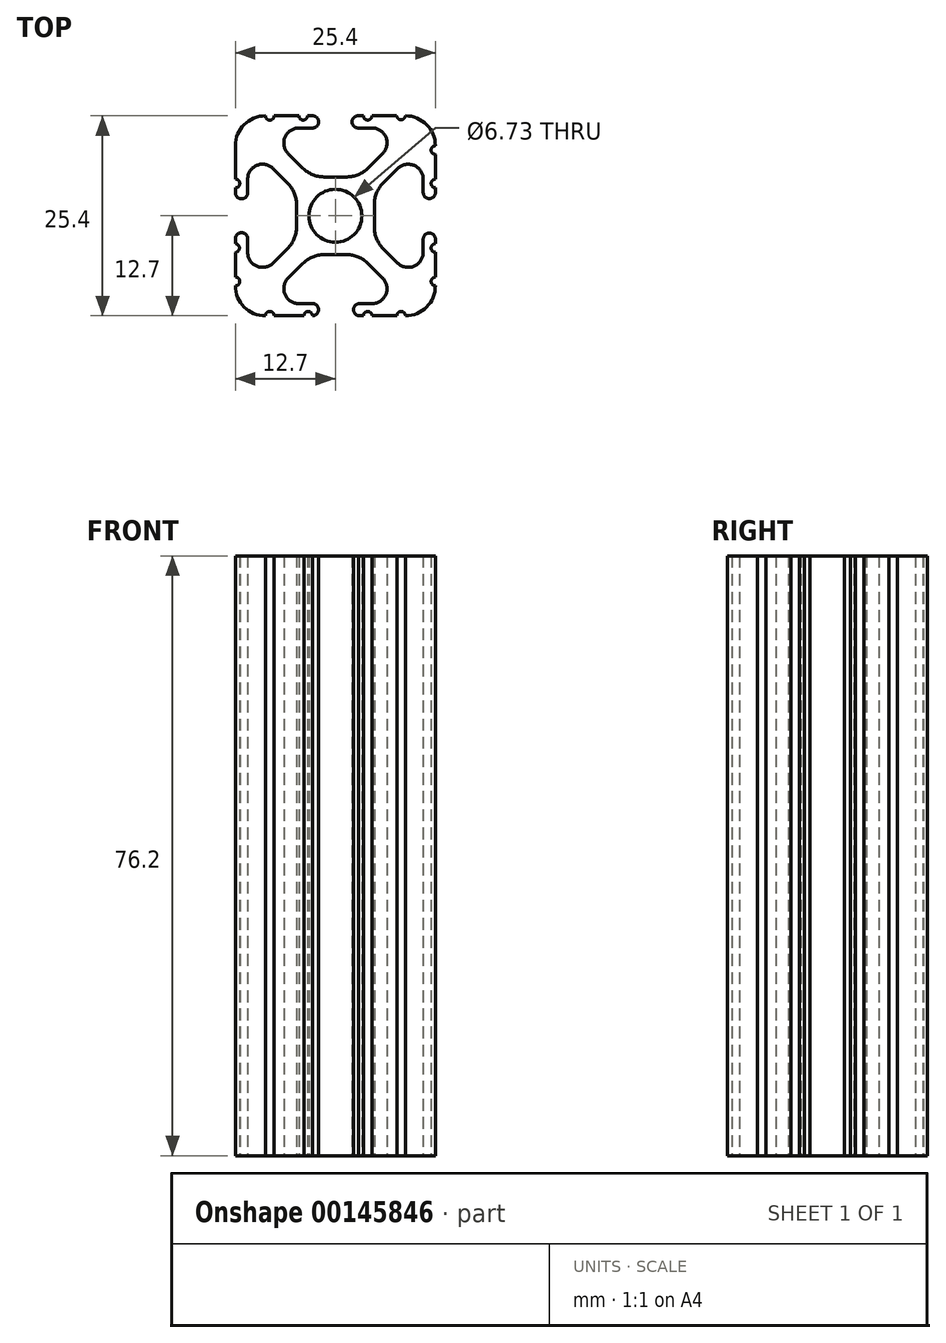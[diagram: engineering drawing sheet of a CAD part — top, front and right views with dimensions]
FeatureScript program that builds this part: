
annotation { "Feature Type Name" : "Feature", "Feature Type Description" : "" }
export const myFeature = defineFeature(function(context is Context, id is Id, definition is map)
    precondition{}
    {
        {
            var Q0;
            Q0=qCreatedBy(makeId("Top.planeOp"),FACE);
            var sketch = newSketch(context, id + "F0", { "sketchPlane" : qUnion([Q0])});
            skCircle(sketch, "E0", {"center": v(-12.7, 12.7) * mm, "radius": 3.36 * mm});
            skLineSegment(sketch, "E1.bottom", {"start": v(-11.24, 17.64) * mm, "end": v(-14.16, 17.64) * mm});
            skLineSegment(sketch, "E1.top", {"start": v(-11.24, 7.76) * mm, "end": v(-14.16, 7.76) * mm});
            skLineSegment(sketch, "E1.left", {"start": v(-7.76, 14.16) * mm, "end": v(-7.76, 11.24) * mm});
            skLineSegment(sketch, "E1.right", {"start": v(-17.64, 14.16) * mm, "end": v(-17.64, 11.24) * mm});
            skPoint(sketch, "E2.visualSharp", {"position": v(-25.4, 25.4) * mm});
            skPoint(sketch, "E3.visualSharp", {"position": v(0, 25.4) * mm});
            skPoint(sketch, "E4.visualSharp", {"position": v(0, 0) * mm});
            skPoint(sketch, "E5.visualSharp", {"position": v(-25.4, 0) * mm});
            skLineSegment(sketch, "E6.0", {"start": v(-18.7, 20.6) * mm, "end": v(-16.85, 18.76) * mm});
            skLineSegment(sketch, "E7.0", {"start": v(-20.6, 18.7) * mm, "end": v(-18.76, 16.85) * mm});
            skPoint(sketch, "E8.orphan", {"position": v(-23.85, 1.55) * mm});
            skPoint(sketch, "E9.orphan", {"position": v(-23.85, 23.85) * mm});
            skPoint(sketch, "E10.orphan", {"position": v(-1.55, 23.85) * mm});
            skPoint(sketch, "E11.orphan", {"position": v(-1.55, 1.55) * mm});
            skLineSegment(sketch, "E12", {"start": v(-8.55, 6.64) * mm, "end": v(-6.7, 4.8) * mm});
            skLineSegment(sketch, "E13.0", {"start": v(-18.7, 4.8) * mm, "end": v(-16.85, 6.64) * mm});
            skLineSegment(sketch, "E14.0", {"start": v(-20.6, 6.7) * mm, "end": v(-18.76, 8.55) * mm});
            skLineSegment(sketch, "E15.0", {"start": v(-8.55, 18.76) * mm, "end": v(-6.7, 20.6) * mm});
            skPoint(sketch, "E16.visualSharp", {"position": v(-23.85, 21.95) * mm});
            skArc(sketch, "E16.filletArc", {"start": v(-20.6, 18.7) * mm, "mid": v(-22.68, 19.1) * mm, "end": v(-23.85, 17.35) * mm});
            skPoint(sketch, "E17.visualSharp", {"position": v(-21.95, 23.85) * mm});
            skArc(sketch, "E17.filletArc", {"start": v(-17.35, 23.85) * mm, "mid": v(-19.1, 22.68) * mm, "end": v(-18.7, 20.6) * mm});
            skPoint(sketch, "E18.visualSharp", {"position": v(-5.34, 23.85) * mm});
            skLineSegment(sketch, "E19", {"start": v(-17.35, 23.85) * mm, "end": v(-15.58, 23.85) * mm});
            skLineSegment(sketch, "E20", {"start": v(-23.85, 17.35) * mm, "end": v(-23.85, 15.62) * mm});
            skLineSegment(sketch, "E21", {"start": v(-8.05, 1.55) * mm, "end": v(-9.78, 1.55) * mm});
            skArc(sketch, "E22.filletArc", {"start": v(-6.7, 20.6) * mm, "mid": v(-6.3, 22.68) * mm, "end": v(-8.05, 23.85) * mm});
            skPoint(sketch, "E23.visualSharp", {"position": v(-1.55, 3.45) * mm});
            skPoint(sketch, "E24.visualSharp", {"position": v(-3.45, 1.55) * mm});
            skArc(sketch, "E24.filletArc", {"start": v(-8.05, 1.55) * mm, "mid": v(-6.3, 2.73) * mm, "end": v(-6.7, 4.8) * mm});
            skArc(sketch, "E25.filletArc", {"start": v(-18.7, 4.8) * mm, "mid": v(-19.1, 2.73) * mm, "end": v(-17.35, 1.55) * mm});
            skArc(sketch, "E26.filletArc", {"start": v(-23.85, 8.05) * mm, "mid": v(-22.68, 6.3) * mm, "end": v(-20.6, 6.7) * mm});
            skLineSegment(sketch, "E27.bottom", {"start": v(-4.9, 0) * mm, "end": v(-8.05, 0) * mm});
            skLineSegment(sketch, "E27.top", {"start": v(-4.92, 25.4) * mm, "end": v(-8.05, 25.4) * mm});
            skLineSegment(sketch, "E27.left", {"start": v(0, 4.9) * mm, "end": v(0, 8.05) * mm});
            skLineSegment(sketch, "E27.right", {"start": v(-25.4, 4.9) * mm, "end": v(-25.4, 8.05) * mm});
            skArc(sketch, "E28.filletArc", {"start": v(-25.4, 3.81) * mm, "mid": v(-24.28, 1.12) * mm, "end": v(-21.59, 0) * mm});
            skArc(sketch, "E29.filletArc", {"start": v(-3.81, 0) * mm, "mid": v(-1.12, 1.12) * mm, "end": v(0, 3.8) * mm});
            skArc(sketch, "E30.filletArc", {"start": v(0, 21.59) * mm, "mid": v(-1.12, 24.28) * mm, "end": v(-3.8, 25.4) * mm});
            skArc(sketch, "E31.filletArc", {"start": v(-21.59, 25.4) * mm, "mid": v(-24.28, 24.28) * mm, "end": v(-25.4, 21.59) * mm});
            skPoint(sketch, "E32.newPointA", {"position": v(-17.64, 7.76) * mm});
            skArc(sketch, "E32.filletArc", {"start": v(-14.16, 7.76) * mm, "mid": v(-15.62, 7.47) * mm, "end": v(-16.85, 6.64) * mm});
            skPoint(sketch, "E33.newPointA", {"position": v(-7.76, 7.76) * mm});
            skArc(sketch, "E33.filletArc", {"start": v(-8.55, 6.64) * mm, "mid": v(-9.78, 7.47) * mm, "end": v(-11.24, 7.76) * mm});
            skArc(sketch, "E34.filletArc", {"start": v(-7.76, 11.24) * mm, "mid": v(-7.47, 9.78) * mm, "end": v(-6.64, 8.55) * mm});
            skArc(sketch, "E35.filletArc", {"start": v(-6.64, 16.85) * mm, "mid": v(-7.47, 15.62) * mm, "end": v(-7.76, 14.16) * mm});
            skPoint(sketch, "E36.newPointB", {"position": v(-7.76, 17.64) * mm});
            skArc(sketch, "E36.filletArc", {"start": v(-11.24, 17.64) * mm, "mid": v(-9.78, 17.93) * mm, "end": v(-8.55, 18.76) * mm});
            skPoint(sketch, "E37.newPointB", {"position": v(-17.64, 17.64) * mm});
            skArc(sketch, "E37.filletArc", {"start": v(-16.85, 18.76) * mm, "mid": v(-15.62, 17.93) * mm, "end": v(-14.16, 17.64) * mm});
            skArc(sketch, "E38.filletArc", {"start": v(-17.64, 14.16) * mm, "mid": v(-17.93, 15.62) * mm, "end": v(-18.76, 16.85) * mm});
            skArc(sketch, "E39.filletArc", {"start": v(-18.76, 8.55) * mm, "mid": v(-17.93, 9.78) * mm, "end": v(-17.64, 11.24) * mm});
            skLineSegment(sketch, "E40", {"start": v(-6.64, 8.55) * mm, "end": v(-4.8, 6.7) * mm});
            skPoint(sketch, "E41.visualSharp", {"position": v(-1.55, 21.95) * mm});
            skArc(sketch, "E42.filletArc", {"start": v(-4.8, 6.7) * mm, "mid": v(-2.73, 6.3) * mm, "end": v(-1.55, 8.05) * mm});
            skLineSegment(sketch, "E43", {"start": v(-1.55, 8.05) * mm, "end": v(-1.55, 9.78) * mm});
            skLineSegment(sketch, "E44", {"start": v(-6.64, 16.85) * mm, "end": v(-4.8, 18.7) * mm});
            skArc(sketch, "E45.filletArc", {"start": v(-1.55, 17.35) * mm, "mid": v(-2.73, 19.1) * mm, "end": v(-4.8, 18.7) * mm});
            skArc(sketch, "E46", {"start": v(-23.85, 9.78) * mm, "mid": v(-24.63, 10.56) * mm, "end": v(-25.4, 9.78) * mm});
            skArc(sketch, "E47", {"start": v(-25.4, 15.62) * mm, "mid": v(-24.63, 14.86) * mm, "end": v(-23.85, 15.62) * mm});
            skArc(sketch, "E48", {"start": v(-15.62, 23.85) * mm, "mid": v(-14.83, 24.63) * mm, "end": v(-15.62, 25.4) * mm});
            skArc(sketch, "E49", {"start": v(-9.78, 25.4) * mm, "mid": v(-10.6, 24.63) * mm, "end": v(-9.78, 23.85) * mm});
            skArc(sketch, "E50", {"start": v(-1.55, 15.62) * mm, "mid": v(-0.77, 14.88) * mm, "end": v(0, 15.62) * mm});
            skArc(sketch, "E51", {"start": v(0, 9.78) * mm, "mid": v(-0.77, 10.5) * mm, "end": v(-1.55, 9.78) * mm});
            skArc(sketch, "E52", {"start": v(-9.78, 1.55) * mm, "mid": v(-10.4, 0.77) * mm, "end": v(-9.78, 0) * mm});
            skArc(sketch, "E53", {"start": v(-15.62, 0) * mm, "mid": v(-14.85, 0.77) * mm, "end": v(-15.62, 1.55) * mm});
            skLineSegment(sketch, "E54.trimOffspring", {"start": v(-15.62, 1.55) * mm, "end": v(-17.35, 1.55) * mm});
            skLineSegment(sketch, "E55.trimOffspring", {"start": v(-16.7, 0) * mm, "end": v(-20.5, 0) * mm});
            skLineSegment(sketch, "E56.trimOffspring", {"start": v(-1.55, 15.62) * mm, "end": v(-1.55, 17.35) * mm});
            skLineSegment(sketch, "E57.trimOffspring", {"start": v(0, 15.62) * mm, "end": v(0, 16.26) * mm});
            skLineSegment(sketch, "E58.trimOffspring", {"start": v(-23.85, 9.78) * mm, "end": v(-23.85, 8.05) * mm});
            skLineSegment(sketch, "E59.trimOffspring", {"start": v(-25.4, 15.62) * mm, "end": v(-25.4, 16.26) * mm});
            skLineSegment(sketch, "E60.trimOffspring", {"start": v(-9.86, 23.85) * mm, "end": v(-8.05, 23.85) * mm});
            skLineSegment(sketch, "E61.trimOffspring", {"start": v(-15.58, 25.4) * mm, "end": v(-16.25, 25.4) * mm});
            skPoint(sketch, "E62.start.orphan", {"position": v(-15.62, 17.93) * mm});
            skPoint(sketch, "E63.start.orphan", {"position": v(-9.78, 17.93) * mm});
            skPoint(sketch, "E64.start.orphan", {"position": v(-7.47, 15.62) * mm});
            skPoint(sketch, "E65.start.orphan", {"position": v(-7.47, 9.78) * mm});
            skPoint(sketch, "E66.start.orphan", {"position": v(-17.93, 15.62) * mm});
            skPoint(sketch, "E67.start.orphan", {"position": v(-17.93, 9.78) * mm});
            skPoint(sketch, "E68.start.orphan", {"position": v(-9.78, 7.47) * mm});
            skPoint(sketch, "E69.start.orphan", {"position": v(-15.62, 7.47) * mm});
            skPoint(sketch, "E70.endSnap0", {"position": v(0, 18.6) * mm});
            skPoint(sketch, "E71.startSnap0", {"position": v(-1.55, 8.92) * mm});
            skArc(sketch, "E72", {"start": v(-4.92, 25.4) * mm, "mid": v(-4.37, 24.9) * mm, "end": v(-3.81, 25.4) * mm});
            skArc(sketch, "E73", {"start": v(-9.14, 25.4) * mm, "mid": v(-8.6, 24.86) * mm, "end": v(-8.05, 25.4) * mm});
            skArc(sketch, "E74", {"start": v(-17.35, 25.4) * mm, "mid": v(-16.8, 24.86) * mm, "end": v(-16.25, 25.4) * mm});
            skArc(sketch, "E75", {"start": v(-21.59, 25.4) * mm, "mid": v(-21.04, 24.85) * mm, "end": v(-20.49, 25.4) * mm});
            skLineSegment(sketch, "E76", {"start": v(-25.4, 21.59) * mm, "end": v(-25.4, 20.5) * mm});
            skArc(sketch, "E77", {"start": v(-25.4, 16.26) * mm, "mid": v(-24.84, 16.8) * mm, "end": v(-25.4, 17.35) * mm});
            skArc(sketch, "E78", {"start": v(-25.4, 8.05) * mm, "mid": v(-24.9, 8.6) * mm, "end": v(-25.4, 9.15) * mm});
            skArc(sketch, "E79", {"start": v(-25.4, 3.81) * mm, "mid": v(-24.85, 4.36) * mm, "end": v(-25.4, 4.9) * mm});
            skArc(sketch, "E80", {"start": v(-20.5, 0) * mm, "mid": v(-21.04, 0.55) * mm, "end": v(-21.59, 0) * mm});
            skArc(sketch, "E81", {"start": v(-15.62, 0) * mm, "mid": v(-16.16, 0.54) * mm, "end": v(-16.7, 0) * mm});
            skArc(sketch, "E82", {"start": v(-8.05, 0) * mm, "mid": v(-8.6, 0.55) * mm, "end": v(-9.15, 0) * mm});
            skArc(sketch, "E83", {"start": v(-3.81, 0) * mm, "mid": v(-4.35, 0.54) * mm, "end": v(-4.9, 0) * mm});
            skLineSegment(sketch, "E84.trimOffspring", {"start": v(-17.35, 25.4) * mm, "end": v(-20.49, 25.4) * mm});
            skLineSegment(sketch, "E85.trimOffspring", {"start": v(-25.4, 17.35) * mm, "end": v(-25.4, 21.59) * mm});
            skLineSegment(sketch, "E86.trimOffspring", {"start": v(-25.4, 9.15) * mm, "end": v(-25.4, 9.78) * mm});
            skLineSegment(sketch, "E87.trimOffspring", {"start": v(-9.15, 0) * mm, "end": v(-9.78, 0) * mm});
            skArc(sketch, "E88", {"start": v(0, 4.9) * mm, "mid": v(-0.54, 4.36) * mm, "end": v(0, 3.8) * mm});
            skArc(sketch, "E89", {"start": v(0, 9.15) * mm, "mid": v(-0.54, 8.6) * mm, "end": v(0, 8.05) * mm});
            skLineSegment(sketch, "E90.trimOffspring", {"start": v(0, 9.15) * mm, "end": v(0, 9.78) * mm});
            skArc(sketch, "E91", {"start": v(0, 21.59) * mm, "mid": v(-0.55, 21.04) * mm, "end": v(0, 20.5) * mm});
            skArc(sketch, "E92", {"start": v(0, 17.35) * mm, "mid": v(-0.55, 16.8) * mm, "end": v(0, 16.26) * mm});
            skLineSegment(sketch, "E93.trimOffspring", {"start": v(0, 17.35) * mm, "end": v(0, 20.5) * mm});
            skLineSegment(sketch, "E94.trimOffspring", {"start": v(-9.14, 25.4) * mm, "end": v(-9.86, 25.4) * mm});
            skSolve(sketch);
        }
        {
            var Q0;
            Q0 = qSketchRegion(id + "F0", true);
            extrude(context, id + "F1", {"entities" : qUnion([Q0]), "depth" : 76.2 * mm});
        }
    });
